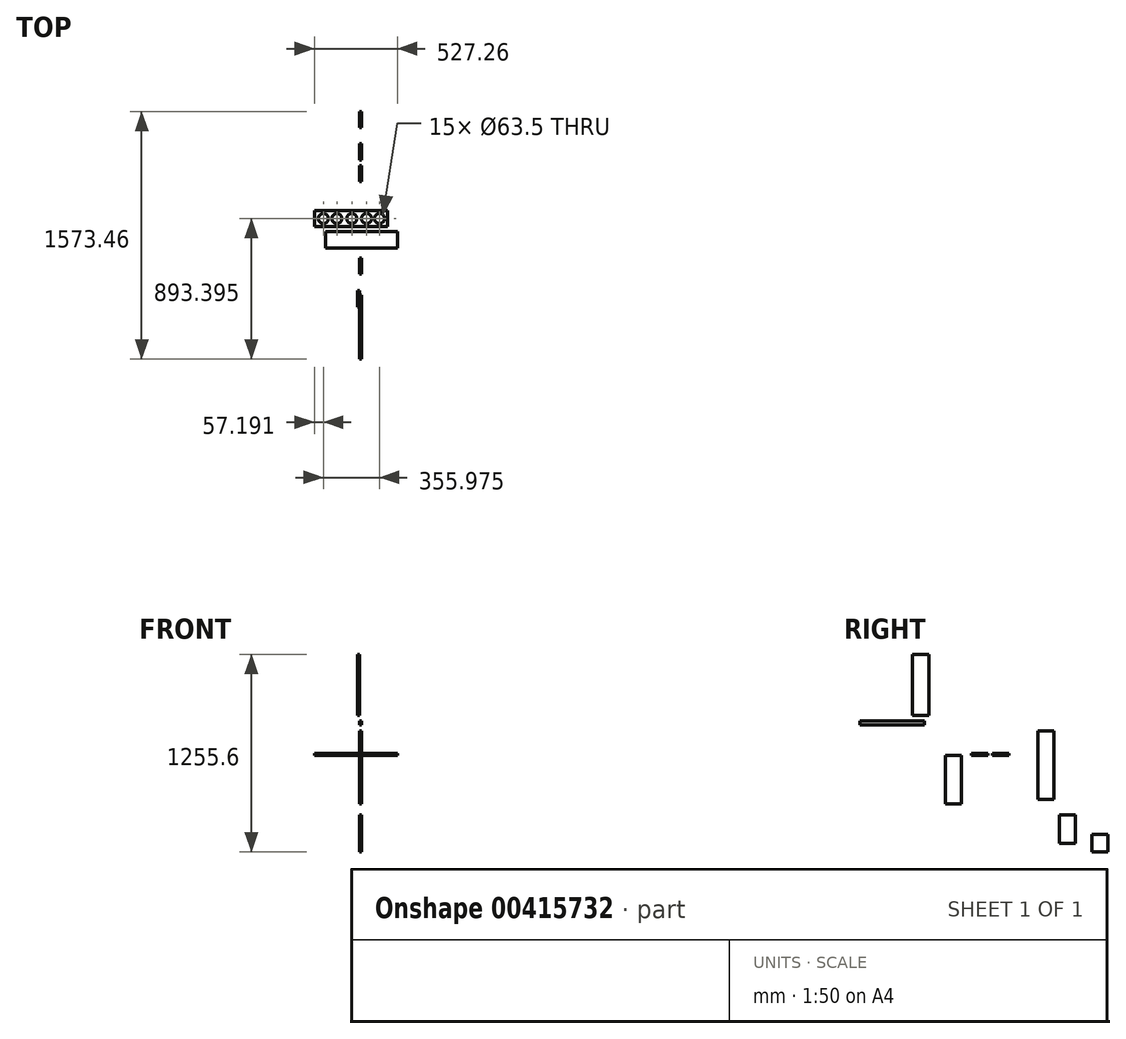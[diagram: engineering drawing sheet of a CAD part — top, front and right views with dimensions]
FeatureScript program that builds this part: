
annotation { "Feature Type Name" : "Feature", "Feature Type Description" : "" }
export const myFeature = defineFeature(function(context is Context, id is Id, definition is map)
    precondition{}
    {
        {
            var Q0;
            Q0=qCreatedBy(makeId("Top.planeOp"),FACE);
            var sketch = newSketch(context, id + "F0", { "sketchPlane" : qUnion([Q0])});
            skLineSegment(sketch, "E0.bottom", {"start": v(-286.38, -9.7) * mm, "end": v(178, -9.7) * mm});
            skLineSegment(sketch, "E0.top", {"start": v(-286.38, -111.97) * mm, "end": v(178, -111.97) * mm});
            skLineSegment(sketch, "E0.left", {"start": v(-286.38, -9.7) * mm, "end": v(-286.38, -111.97) * mm});
            skLineSegment(sketch, "E0.right", {"start": v(178, -9.7) * mm, "end": v(178, -111.97) * mm});
            skSolve(sketch);
        }
        {
            var Q0;
            Q0=makeQuery(id+"F0.imprint","IMPRINT",FACE,{"disambiguationData":[TD([[makeQuery(id+"F0.imprint","IMPRINT",EDGE,{"derivedFrom":sQuery(id+"F0.wireOp",EDGE,"E0.bottom")}),-1.0]])]});
            extrude(context, id + "F1", {"entities" : qUnion([Q0]), "depth" : 12.7 * mm});
        }
        {
            var Q0;
            Q0=makeQuery(id+"F1.opExtrude","CAP_FACE",FACE,{"disambiguationData":[OSD([sQuery(id+"F0.wireOp",EDGE,"E0.bottom"),sQuery(id+"F0.wireOp",EDGE,"E0.top"),sQuery(id+"F0.wireOp",EDGE,"E0.left"),sQuery(id+"F0.wireOp",EDGE,"E0.right")])],"isStart":false});
            var sketch = newSketch(context, id + "F2", { "sketchPlane" : qUnion([Q0])});
            skPoint(sketch, "E1", {"position": v(-48.7, -59.76) * mm});
            skPoint(sketch, "E2", {"position": v(-229.19, -59.76) * mm});
            skPoint(sketch, "E3", {"position": v(-143.44, -59.76) * mm});
            skPoint(sketch, "E4", {"position": v(45.02, -59.76) * mm});
            skPoint(sketch, "E5", {"position": v(126.79, -59.76) * mm});
            skSolve(sketch);
        }
        {
            var Q0;
            Q0=sQuery(id+"F2.wireOp",VERTEX,"E2");
            var Q1;
            Q1=sQuery(id+"F2.wireOp",VERTEX,"E3");
            var Q2;
            Q2=sQuery(id+"F2.wireOp",VERTEX,"E1");
            var Q3;
            Q3=sQuery(id+"F2.wireOp",VERTEX,"E4");
            var Q4;
            Q4=sQuery(id+"F2.wireOp",VERTEX,"E5");
            var Q5;
            Q5=makeQuery(id+"F1.opExtrude","SWEPT_BODY",BODY,{"disambiguationData":[OSD([sQuery(id+"F0.wireOp",EDGE,"E0.bottom"),sQuery(id+"F0.wireOp",EDGE,"E0.top"),sQuery(id+"F0.wireOp",EDGE,"E0.left"),sQuery(id+"F0.wireOp",EDGE,"E0.right")])]});
            hole(context, id + "F3", {"style" : HoleStyle.SIMPLE, "endStyle" : HoleEndStyle.THROUGH, "holeDiameter" : 63.5 * mm, "isTappedThrough" : true, "tappedDepth" : 12.7 * mm, "tapClearance" : 3, "locations" : qUnion([Q0, Q1, Q2, Q3, Q4]), "scope" : qUnion([Q5])});
        }
        {
            var Q0;
            Q0=qCreatedBy(makeId("Top.planeOp"),FACE);
            var sketch = newSketch(context, id + "F4", { "sketchPlane" : qUnion([Q0])});
            skLineSegment(sketch, "E6.bottom", {"start": v(-215.17, -143.02) * mm, "end": v(240.88, -143.02) * mm});
            skLineSegment(sketch, "E6.top", {"start": v(-215.17, -246.65) * mm, "end": v(240.88, -246.65) * mm});
            skLineSegment(sketch, "E6.left", {"start": v(-215.17, -143.02) * mm, "end": v(-215.17, -246.65) * mm});
            skLineSegment(sketch, "E6.right", {"start": v(240.88, -143.02) * mm, "end": v(240.88, -246.65) * mm});
            skSolve(sketch);
        }
        {
            var Q0;
            Q0=makeQuery(id+"F4.imprint","IMPRINT",FACE,{"disambiguationData":[TD([[makeQuery(id+"F4.imprint","IMPRINT",EDGE,{"derivedFrom":sQuery(id+"F4.wireOp",EDGE,"E6.bottom")}),-1.0]])]});
            extrude(context, id + "F5", {"entities" : qUnion([Q0]), "depth" : 12.7 * mm});
        }
        {
            var Q0;
            Q0=qCreatedBy(makeId("Right.planeOp"),FACE);
            var sketch = newSketch(context, id + "F6", { "sketchPlane" : qUnion([Q0])});
            skLineSegment(sketch, "E7.bottom", {"start": v(175.3, -278.49) * mm, "end": v(276.5, -278.49) * mm});
            skLineSegment(sketch, "E7.top", {"start": v(175.3, 154.65) * mm, "end": v(276.5, 154.65) * mm});
            skLineSegment(sketch, "E7.left", {"start": v(175.3, -278.49) * mm, "end": v(175.3, 154.65) * mm});
            skLineSegment(sketch, "E7.right", {"start": v(276.5, -278.49) * mm, "end": v(276.5, 154.65) * mm});
            skSolve(sketch);
        }
        {
            var Q0;
            Q0 = qSketchRegion(id + "F6", true);
            extrude(context, id + "F7", {"entities" : qUnion([Q0]), "depth" : 12.7 * mm});
        }
        {
            var Q0;
            Q0=qCreatedBy(makeId("Right.planeOp"),FACE);
            var sketch = newSketch(context, id + "F8", { "sketchPlane" : qUnion([Q0])});
            skLineSegment(sketch, "E8.bottom", {"start": v(-620.2, 253.78) * mm, "end": v(-516.42, 253.78) * mm});
            skLineSegment(sketch, "E8.top", {"start": v(-620.2, 641.25) * mm, "end": v(-516.42, 641.25) * mm});
            skLineSegment(sketch, "E8.left", {"start": v(-620.2, 253.78) * mm, "end": v(-620.2, 641.25) * mm});
            skLineSegment(sketch, "E8.right", {"start": v(-516.42, 253.78) * mm, "end": v(-516.42, 641.25) * mm});
            skSolve(sketch);
        }
        {
            var Q0;
            Q0=makeQuery(id+"F8.imprint","IMPRINT",FACE,{"disambiguationData":[TD([[makeQuery(id+"F8.imprint","IMPRINT",EDGE,{"derivedFrom":sQuery(id+"F8.wireOp",EDGE,"E8.bottom")}),1.0]])]});
            extrude(context, id + "F9", {"entities" : qUnion([Q0]), "oppositeDirection" : true, "depth" : 12.7 * mm});
        }
        {
            var Q0;
            Q0=qCreatedBy(makeId("Right.planeOp"),FACE);
            var sketch = newSketch(context, id + "F10", { "sketchPlane" : qUnion([Q0])});
            skLineSegment(sketch, "E9.bottom", {"start": v(-412.57, 0) * mm, "end": v(-309.88, 0) * mm});
            skLineSegment(sketch, "E9.top", {"start": v(-412.57, -307.93) * mm, "end": v(-309.88, -307.93) * mm});
            skLineSegment(sketch, "E9.left", {"start": v(-412.57, 0) * mm, "end": v(-412.57, -307.93) * mm});
            skLineSegment(sketch, "E9.right", {"start": v(-309.88, 0) * mm, "end": v(-309.88, -307.93) * mm});
            skLineSegment(sketch, "E10.bottom", {"start": v(312.25, -378.38) * mm, "end": v(414.94, -378.38) * mm});
            skLineSegment(sketch, "E10.top", {"start": v(312.25, -558.75) * mm, "end": v(414.94, -558.75) * mm});
            skLineSegment(sketch, "E10.left", {"start": v(312.25, -378.38) * mm, "end": v(312.25, -558.75) * mm});
            skLineSegment(sketch, "E10.right", {"start": v(414.94, -378.38) * mm, "end": v(414.94, -558.75) * mm});
            skSolve(sketch);
        }
        {
            var Q0;
            Q0 = qSketchRegion(id + "F10", true);
            extrude(context, id + "F11", {"entities" : qUnion([Q0]), "depth" : 12.7 * mm});
        }
        {
            var Q0;
            Q0=qCreatedBy(makeId("Right.planeOp"),FACE);
            var sketch = newSketch(context, id + "F12", { "sketchPlane" : qUnion([Q0])});
            skLineSegment(sketch, "E11.bottom", {"start": v(517.62, -501.99) * mm, "end": v(620.3, -501.99) * mm});
            skLineSegment(sketch, "E11.top", {"start": v(517.62, -614.35) * mm, "end": v(620.3, -614.35) * mm});
            skLineSegment(sketch, "E11.left", {"start": v(517.62, -501.99) * mm, "end": v(517.62, -614.35) * mm});
            skLineSegment(sketch, "E11.right", {"start": v(620.3, -501.99) * mm, "end": v(620.3, -614.35) * mm});
            skSolve(sketch);
        }
        {
            var Q0;
            Q0 = qSketchRegion(id + "F12", true);
            extrude(context, id + "F13", {"entities" : qUnion([Q0]), "depth" : 12.7 * mm});
        }
        {
            var Q0;
            Q0=qCreatedBy(makeId("Right.planeOp"),FACE);
            var sketch = newSketch(context, id + "F14", { "sketchPlane" : qUnion([Q0])});
            skLineSegment(sketch, "E12.bottom", {"start": v(-953.16, 217.71) * mm, "end": v(-545.45, 217.71) * mm});
            skLineSegment(sketch, "E12.top", {"start": v(-953.16, 193.45) * mm, "end": v(-545.45, 193.45) * mm});
            skLineSegment(sketch, "E12.left", {"start": v(-953.16, 217.71) * mm, "end": v(-953.16, 193.45) * mm});
            skLineSegment(sketch, "E12.right", {"start": v(-545.45, 217.71) * mm, "end": v(-545.45, 193.45) * mm});
            skSolve(sketch);
        }
        {
            var Q0;
            Q0=makeQuery(id+"F14.imprint","IMPRINT",FACE,{"disambiguationData":[TD([[makeQuery(id+"F14.imprint","IMPRINT",EDGE,{"derivedFrom":sQuery(id+"F14.wireOp",EDGE,"E12.bottom")}),-1.0]])]});
            extrude(context, id + "F15", {"entities" : qUnion([Q0]), "depth" : 12.7 * mm});
        }
    });
